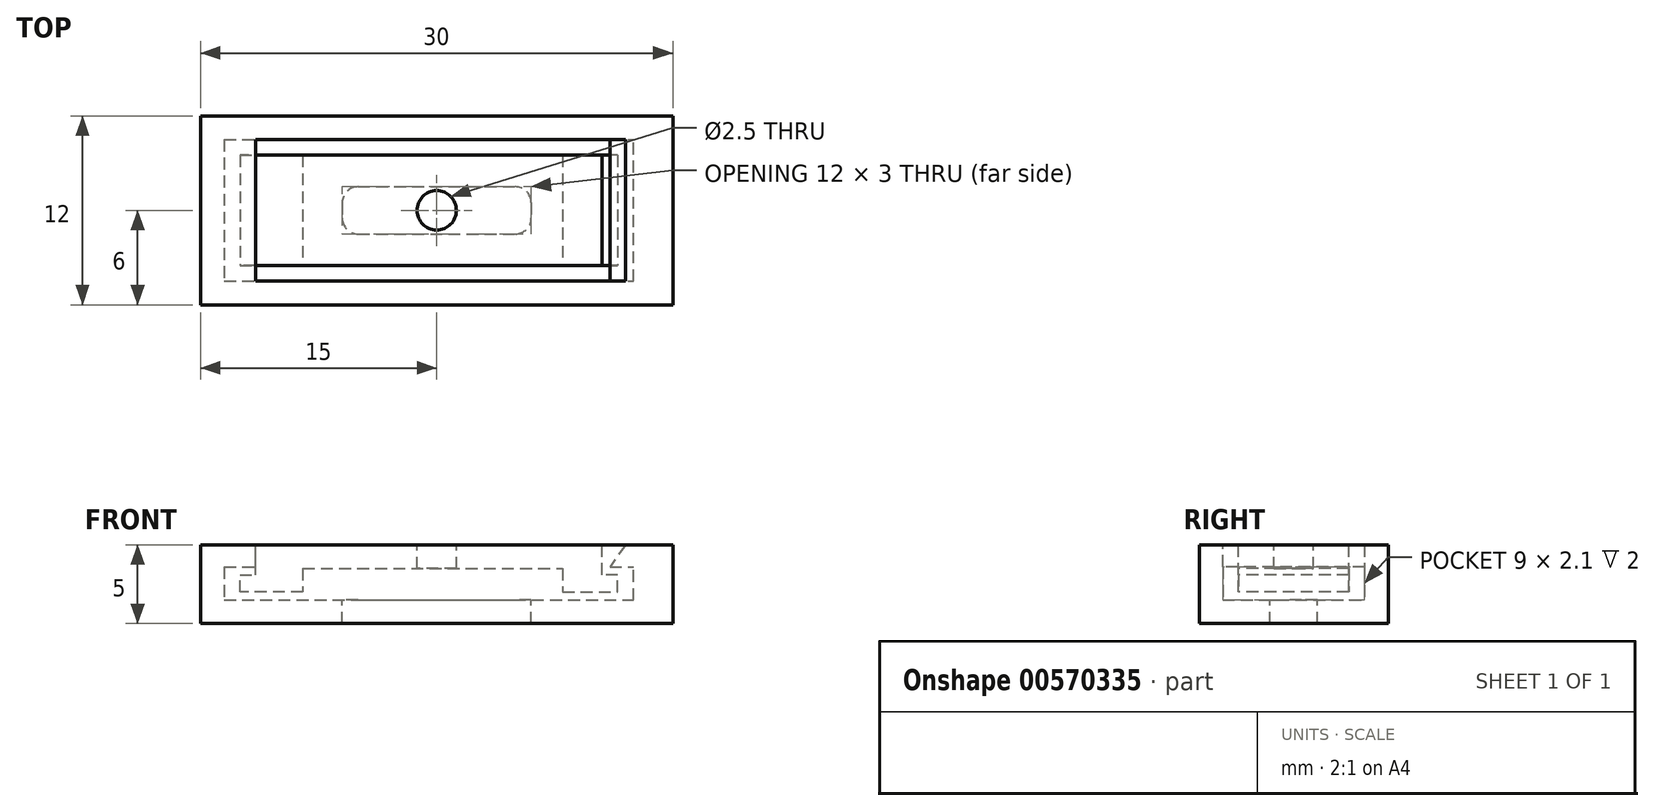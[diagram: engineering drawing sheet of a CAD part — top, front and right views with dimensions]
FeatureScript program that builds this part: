
annotation { "Feature Type Name" : "Feature", "Feature Type Description" : "" }
export const myFeature = defineFeature(function(context is Context, id is Id, definition is map)
    precondition{}
    {
        {
            var Q0;
            Q0=qCreatedBy(makeId("Top.planeOp"),FACE);
            var sketch = newSketch(context, id + "F0", { "sketchPlane" : qUnion([Q0])});
            skLineSegment(sketch, "E0.bottom", {"start": v(-15, 6) * mm, "end": v(15, 6) * mm});
            skLineSegment(sketch, "E0.top", {"start": v(-15, -6) * mm, "end": v(15, -6) * mm});
            skLineSegment(sketch, "E0.left", {"start": v(-15, 6) * mm, "end": v(-15, -6) * mm});
            skLineSegment(sketch, "E0.right", {"start": v(15, 6) * mm, "end": v(15, -6) * mm});
            skPoint(sketch, "E0.middle", {"position": v(0, 0) * mm});
            skSolve(sketch);
        }
        {
            var Q0;
            Q0 = qSketchRegion(id + "F0", true);
            extrude(context, id + "F1", {"entities" : qUnion([Q0]), "depth" : 5 * mm, "offsetDistance" : 25 * mm});
        }
        {
            var Q0;
            Q0=makeQuery(id+"F1.opExtrude","CAP_FACE",FACE,{"disambiguationData":[OSD([sQuery(id+"F0.wireOp",EDGE,"E0.bottom"),sQuery(id+"F0.wireOp",EDGE,"E0.top"),sQuery(id+"F0.wireOp",EDGE,"E0.left"),sQuery(id+"F0.wireOp",EDGE,"E0.right")])],"isStart":false});
            shell(context, id + "F2", {"entities" : qUnion([Q0]), "thickness" : 1.5 * mm});
        }
        {
            var Q0;
            Q0=makeQuery(id+"F1.opExtrude","CAP_FACE",FACE,{"disambiguationData":[OSD([sQuery(id+"F0.wireOp",EDGE,"E0.bottom"),sQuery(id+"F0.wireOp",EDGE,"E0.top"),sQuery(id+"F0.wireOp",EDGE,"E0.left"),sQuery(id+"F0.wireOp",EDGE,"E0.right")])],"isStart":false});
            var sketch = newSketch(context, id + "F3", { "sketchPlane" : qUnion([Q0])});
            skLineSegment(sketch, "E1.bottom", {"start": v(-13.5, 4.5) * mm, "end": v(-11.5, 4.5) * mm});
            skLineSegment(sketch, "E1.top", {"start": v(-13.5, -4.5) * mm, "end": v(-11.5, -4.5) * mm});
            skLineSegment(sketch, "E1.left", {"start": v(-13.5, 4.5) * mm, "end": v(-13.5, -4.5) * mm});
            skLineSegment(sketch, "E1.right", {"start": v(-11.5, 4.5) * mm, "end": v(-11.5, -4.5) * mm});
            skSolve(sketch);
        }
        {
            var Q0;
            Q0 = qSketchRegion(id + "F3", true);
            extrude(context, id + "F4", {"entities" : qUnion([Q0]), "operationType" : NewBodyOperationType.ADD, "oppositeDirection" : true, "depth" : 1.4 * mm, "offsetDistance" : 25 * mm});
        }
        {
            var Q0;
            Q0=makeQuery(id+"F4.boolean.opBoolean","MERGE",FACE,{"derivedFrom":[makeQuery(id+"F1.opExtrude","CAP_FACE",FACE,{"disambiguationData":[OSD([sQuery(id+"F0.wireOp",EDGE,"E0.bottom"),sQuery(id+"F0.wireOp",EDGE,"E0.top"),sQuery(id+"F0.wireOp",EDGE,"E0.left"),sQuery(id+"F0.wireOp",EDGE,"E0.right")])],"isStart":false}),makeQuery(id+"F4.opExtrude","CAP_FACE",FACE,{"disambiguationData":[OSD([sQuery(id+"F3.wireOp",EDGE,"E1.bottom"),sQuery(id+"F3.wireOp",EDGE,"E1.top"),sQuery(id+"F3.wireOp",EDGE,"E1.left"),sQuery(id+"F3.wireOp",EDGE,"E1.right")])],"isStart":true})]});
            var sketch = newSketch(context, id + "F5", { "sketchPlane" : qUnion([Q0])});
            skLineSegment(sketch, "E2.bottom", {"start": v(13.5, 4.5) * mm, "end": v(12.5, 4.5) * mm});
            skLineSegment(sketch, "E2.top", {"start": v(13.5, -4.5) * mm, "end": v(12.5, -4.5) * mm});
            skLineSegment(sketch, "E2.left", {"start": v(13.5, 4.5) * mm, "end": v(13.5, -4.5) * mm});
            skLineSegment(sketch, "E2.right", {"start": v(12.5, 4.5) * mm, "end": v(12.5, -4.5) * mm});
            skSolve(sketch);
        }
        {
            var Q0;
            Q0 = qSketchRegion(id + "F5", true);
            var Q1;
            Q1=makeQuery(id+"F2.opShell","OFFSET_FACE",FACE,{"disambiguationData":[OSD([sQuery(id+"F0.wireOp",EDGE,"E0.bottom"),sQuery(id+"F0.wireOp",EDGE,"E0.top"),sQuery(id+"F0.wireOp",EDGE,"E0.left"),sQuery(id+"F0.wireOp",EDGE,"E0.right")])]});
            extrude(context, id + "F6", {"entities" : qUnion([Q0]), "operationType" : NewBodyOperationType.ADD, "endBound" : BoundingType.UP_TO_SURFACE, "oppositeDirection" : true, "depth" : 25 * mm, "endBoundEntityFace" : qUnion([Q1]), "offsetDistance" : 25 * mm});
        }
        {
            var Q0;
            Q0=makeQuery(id+"F2.opShell","OFFSET_FACE",FACE,{"disambiguationData":[OSD([sQuery(id+"F0.wireOp",EDGE,"E0.bottom"),sQuery(id+"F0.wireOp",EDGE,"E0.top"),sQuery(id+"F0.wireOp",EDGE,"E0.left"),sQuery(id+"F0.wireOp",EDGE,"E0.right")])]});
            var sketch = newSketch(context, id + "F7", { "sketchPlane" : qUnion([Q0])});
            skLineSegment(sketch, "E3.bottom", {"start": v(-5, 1.5) * mm, "end": v(5, 1.5) * mm});
            skLineSegment(sketch, "E3.top", {"start": v(-5, -1.5) * mm, "end": v(5, -1.5) * mm});
            skLineSegment(sketch, "E3.left", {"start": v(-6, 0.5) * mm, "end": v(-6, -0.5) * mm});
            skLineSegment(sketch, "E3.right", {"start": v(6, 0.5) * mm, "end": v(6, -0.5) * mm});
            skPoint(sketch, "E3.middle", {"position": v(0, 0) * mm});
            skPoint(sketch, "E4.visualSharp", {"position": v(-6, 1.5) * mm});
            skArc(sketch, "E4.filletArc", {"start": v(-5, 1.5) * mm, "mid": v(-5.7, 1.2) * mm, "end": v(-6, 0.5) * mm});
            skPoint(sketch, "E5.visualSharp", {"position": v(6, 1.5) * mm});
            skArc(sketch, "E5.filletArc", {"start": v(6, 0.5) * mm, "mid": v(5.7, 1.2) * mm, "end": v(5, 1.5) * mm});
            skPoint(sketch, "E6.visualSharp", {"position": v(-6, -1.5) * mm});
            skArc(sketch, "E6.filletArc", {"start": v(-6, -0.5) * mm, "mid": v(-5.7, -1.2) * mm, "end": v(-5, -1.5) * mm});
            skPoint(sketch, "E7.visualSharp", {"position": v(6, -1.5) * mm});
            skArc(sketch, "E7.filletArc", {"start": v(5, -1.5) * mm, "mid": v(5.7, -1.2) * mm, "end": v(6, -0.5) * mm});
            skSolve(sketch);
        }
        {
            var Q0;
            Q0 = qSketchRegion(id + "F7", true);
            extrude(context, id + "F8", {"entities" : qUnion([Q0]), "operationType" : NewBodyOperationType.REMOVE, "endBound" : BoundingType.THROUGH_ALL, "oppositeDirection" : true, "depth" : 25 * mm, "offsetDistance" : 25 * mm});
        }
        {
            var Q0;
            Q0=makeQuery(id+"F6.boolean.opBoolean","MERGE",FACE,{"derivedFrom":[makeQuery(id+"F4.boolean.opBoolean","MERGE",FACE,{"derivedFrom":[makeQuery(id+"F1.opExtrude","CAP_FACE",FACE,{"disambiguationData":[OSD([sQuery(id+"F0.wireOp",EDGE,"E0.bottom"),sQuery(id+"F0.wireOp",EDGE,"E0.top"),sQuery(id+"F0.wireOp",EDGE,"E0.left"),sQuery(id+"F0.wireOp",EDGE,"E0.right")])],"isStart":false}),makeQuery(id+"F4.opExtrude","CAP_FACE",FACE,{"disambiguationData":[OSD([sQuery(id+"F3.wireOp",EDGE,"E1.bottom"),sQuery(id+"F3.wireOp",EDGE,"E1.top"),sQuery(id+"F3.wireOp",EDGE,"E1.left"),sQuery(id+"F3.wireOp",EDGE,"E1.right")])],"isStart":true})]}),makeQuery(id+"F6.opExtrude","CAP_FACE",FACE,{"disambiguationData":[OSD([sQuery(id+"F5.wireOp",EDGE,"E2.bottom"),sQuery(id+"F5.wireOp",EDGE,"E2.top"),sQuery(id+"F5.wireOp",EDGE,"E2.left"),sQuery(id+"F5.wireOp",EDGE,"E2.right")])],"isStart":true})]});
            var sketch = newSketch(context, id + "F9", { "sketchPlane" : qUnion([Q0])});
            skLineSegment(sketch, "E8.bottom", {"start": v(12.5, 4.5) * mm, "end": v(11, 4.5) * mm});
            skLineSegment(sketch, "E8.top", {"start": v(12.5, -4.5) * mm, "end": v(11, -4.5) * mm});
            skLineSegment(sketch, "E8.left", {"start": v(12.5, 4.5) * mm, "end": v(12.5, -4.5) * mm});
            skLineSegment(sketch, "E8.right", {"start": v(11, 4.5) * mm, "end": v(11, -4.5) * mm});
            skSolve(sketch);
        }
        {
            var Q0;
            Q0 = qSketchRegion(id + "F9", true);
            extrude(context, id + "F10", {"entities" : qUnion([Q0]), "operationType" : NewBodyOperationType.ADD, "oppositeDirection" : true, "depth" : 1.4 * mm, "offsetDistance" : 25 * mm});
        }
        {
            var Q0;
            Q0=makeQuery(id+"F10.opExtrude","CAP_EDGE",EDGE,{"disambiguationData":[OSD([sQuery(id+"F9.wireOp",EDGE,"E8.right")])],"isStart":true});
            chamfer(context, id + "F11", {"entities" : qUnion([Q0]), "chamferType" : ChamferType.TWO_OFFSETS, "width1" : 1 * mm, "oppositeDirection" : false, "width2" : 1.4 * mm, "tangentPropagation" : true});
        }
        {
            var Q0;
            Q0=makeQuery(id+"F10.boolean.opBoolean","MERGE",FACE,{"derivedFrom":[makeQuery(id+"F6.boolean.opBoolean","MERGE",FACE,{"derivedFrom":[makeQuery(id+"F4.boolean.opBoolean","MERGE",FACE,{"derivedFrom":[makeQuery(id+"F1.opExtrude","CAP_FACE",FACE,{"disambiguationData":[OSD([sQuery(id+"F0.wireOp",EDGE,"E0.bottom"),sQuery(id+"F0.wireOp",EDGE,"E0.top"),sQuery(id+"F0.wireOp",EDGE,"E0.left"),sQuery(id+"F0.wireOp",EDGE,"E0.right")])],"isStart":false}),makeQuery(id+"F4.opExtrude","CAP_FACE",FACE,{"disambiguationData":[OSD([sQuery(id+"F3.wireOp",EDGE,"E1.bottom"),sQuery(id+"F3.wireOp",EDGE,"E1.top"),sQuery(id+"F3.wireOp",EDGE,"E1.left"),sQuery(id+"F3.wireOp",EDGE,"E1.right")])],"isStart":true})]}),makeQuery(id+"F6.opExtrude","CAP_FACE",FACE,{"disambiguationData":[OSD([sQuery(id+"F5.wireOp",EDGE,"E2.bottom"),sQuery(id+"F5.wireOp",EDGE,"E2.top"),sQuery(id+"F5.wireOp",EDGE,"E2.left"),sQuery(id+"F5.wireOp",EDGE,"E2.right")])],"isStart":true})]}),makeQuery(id+"F10.opExtrude","CAP_FACE",FACE,{"disambiguationData":[OSD([sQuery(id+"F9.wireOp",EDGE,"E8.bottom"),sQuery(id+"F9.wireOp",EDGE,"E8.top"),sQuery(id+"F9.wireOp",EDGE,"E8.left"),sQuery(id+"F9.wireOp",EDGE,"E8.right")])],"isStart":true})]});
            var sketch = newSketch(context, id + "F12", { "sketchPlane" : qUnion([Q0])});
            skLineSegment(sketch, "E9.bottom", {"start": v(-11.5, 3.5) * mm, "end": v(10.5, 3.5) * mm});
            skLineSegment(sketch, "E9.top", {"start": v(-11.5, -3.5) * mm, "end": v(10.5, -3.5) * mm});
            skLineSegment(sketch, "E9.left", {"start": v(-11.5, 3.5) * mm, "end": v(-11.5, -3.5) * mm});
            skLineSegment(sketch, "E9.right", {"start": v(10.5, 3.5) * mm, "end": v(10.5, -3.5) * mm});
            skCircle(sketch, "E10", {"center": v(0, 0) * mm, "radius": 1.25 * mm});
            skSolve(sketch);
        }
        {
            var Q0;
            Q0 = qSketchRegion(id + "F12", true);
            extrude(context, id + "F13", {"entities" : qUnion([Q0]), "oppositeDirection" : true, "depth" : 1.5 * mm, "offsetDistance" : 25 * mm});
        }
        {
            var Q0;
            Q0=makeQuery(id+"F13.opExtrude","SWEPT_FACE",FACE,{"disambiguationData":[OSD([sQuery(id+"F12.wireOp",EDGE,"E9.top")])]});
            var sketch = newSketch(context, id + "F14", { "sketchPlane" : qUnion([Q0])});
            skLineSegment(sketch, "E11", {"start": v(-11.5, 3.5) * mm, "end": v(-11.5, 3.1) * mm});
            skLineSegment(sketch, "E12", {"start": v(-11.5, 3.1) * mm, "end": v(-12.5, 3.1) * mm});
            skLineSegment(sketch, "E13", {"start": v(-12.5, 3.1) * mm, "end": v(-12.5, 2) * mm});
            skLineSegment(sketch, "E14", {"start": v(-12.5, 2) * mm, "end": v(-8.5, 2) * mm});
            skLineSegment(sketch, "E15", {"start": v(-8.5, 2) * mm, "end": v(-8.5, 3.5) * mm});
            skLineSegment(sketch, "E16", {"start": v(-8.5, 3.5) * mm, "end": v(-11.5, 3.5) * mm});
            skSolve(sketch);
        }
        {
            var Q0;
            Q0 = qSketchRegion(id + "F14", true);
            var Q1;
            Q1=makeQuery(id+"F13.opExtrude","SWEPT_FACE",FACE,{"disambiguationData":[OSD([sQuery(id+"F12.wireOp",EDGE,"E9.bottom")])]});
            extrude(context, id + "F15", {"entities" : qUnion([Q0]), "operationType" : NewBodyOperationType.ADD, "endBound" : BoundingType.UP_TO_SURFACE, "oppositeDirection" : true, "depth" : 25 * mm, "endBoundEntityFace" : qUnion([Q1]), "offsetDistance" : 25 * mm});
        }
        {
            var Q0;
            Q0=makeQuery(id+"F15.boolean.opBoolean","MERGE",FACE,{"derivedFrom":[makeQuery(id+"F13.opExtrude","SWEPT_FACE",FACE,{"disambiguationData":[OSD([sQuery(id+"F12.wireOp",EDGE,"E9.top")])]}),makeQuery(id+"F15.opExtrude","CAP_FACE",FACE,{"disambiguationData":[OSD([sQuery(id+"F14.wireOp",EDGE,"E11"),sQuery(id+"F14.wireOp",EDGE,"E12"),sQuery(id+"F14.wireOp",EDGE,"E13"),sQuery(id+"F14.wireOp",EDGE,"E14"),sQuery(id+"F14.wireOp",EDGE,"E15"),sQuery(id+"F14.wireOp",EDGE,"E16")])],"isStart":true})]});
            var sketch = newSketch(context, id + "F16", { "sketchPlane" : qUnion([Q0])});
            skLineSegment(sketch, "E17", {"start": v(10.5, 3.5) * mm, "end": v(10.5, 3.1) * mm});
            skLineSegment(sketch, "E18", {"start": v(10.5, 3.1) * mm, "end": v(11.5, 3.1) * mm});
            skLineSegment(sketch, "E19", {"start": v(11.5, 3.1) * mm, "end": v(11.5, 2) * mm});
            skLineSegment(sketch, "E20", {"start": v(11.5, 2) * mm, "end": v(8, 2) * mm});
            skLineSegment(sketch, "E21", {"start": v(8, 2) * mm, "end": v(8, 3.5) * mm});
            skLineSegment(sketch, "E22", {"start": v(8, 3.5) * mm, "end": v(10.5, 3.5) * mm});
            skSolve(sketch);
        }
        {
            var Q0;
            Q0 = qSketchRegion(id + "F16", true);
            var Q1;
            {var subQ0=sQuery(id+"F12.wireOp",EDGE,"E9.bottom");Q1=makeQuery(id+"F15.boolean.opBoolean","MERGE",FACE,{"derivedFrom":[makeQuery(id+"F13.opExtrude","SWEPT_FACE",FACE,{"disambiguationData":[OSD([subQ0])]}),makeQuery(id+"F15.opExtrude","CAP_FACE",FACE,{"disambiguationData":[OSD([subQ0])],"isStart":false})]});}
            extrude(context, id + "F17", {"entities" : qUnion([Q0]), "operationType" : NewBodyOperationType.ADD, "endBound" : BoundingType.UP_TO_SURFACE, "oppositeDirection" : true, "depth" : 25 * mm, "endBoundEntityFace" : qUnion([Q1]), "offsetDistance" : 25 * mm});
        }
    });
